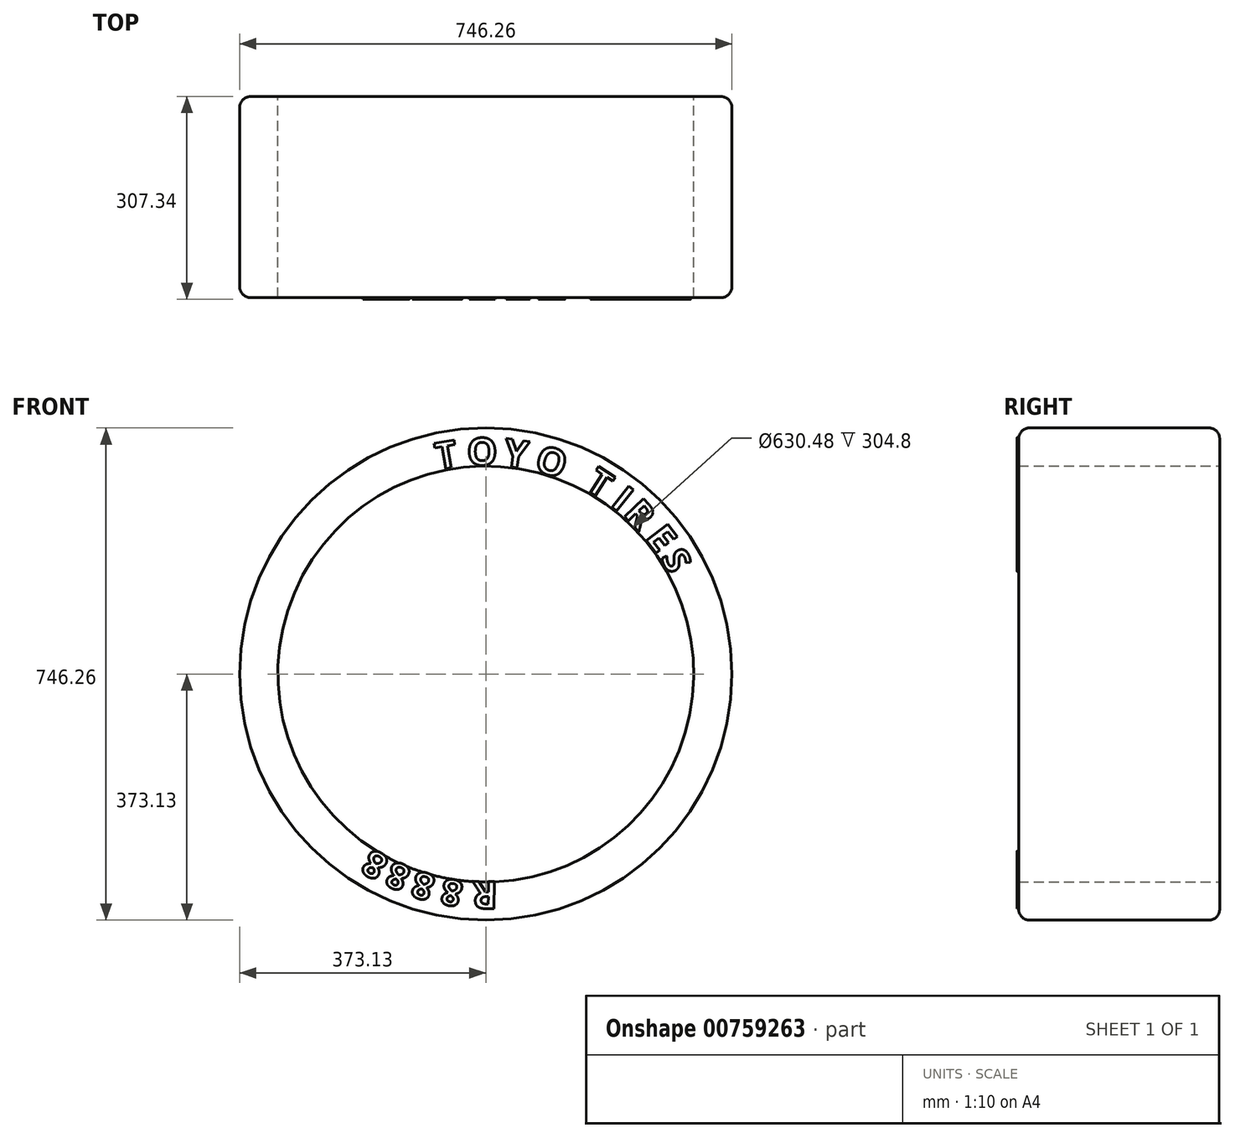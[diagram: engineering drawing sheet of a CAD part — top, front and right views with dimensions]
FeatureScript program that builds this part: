
annotation { "Feature Type Name" : "Feature", "Feature Type Description" : "" }
export const myFeature = defineFeature(function(context is Context, id is Id, definition is map)
    precondition{}
    {
        {
            var Q0;
            Q0=qCreatedBy(makeId("Front.planeOp"),FACE);
            var sketch = newSketch(context, id + "F0", { "sketchPlane" : qUnion([Q0])});
            skCircle(sketch, "E0", {"center": v(0, 0) * mm, "radius": 373.13 * mm});
            skCircle(sketch, "E1", {"center": v(0, 0) * mm, "radius": 315.24 * mm});
            skSolve(sketch);
        }
        {
            var Q0;
            Q0=makeQuery(id+"F0.imprint","IMPRINT",FACE,{"disambiguationData":[TD([[makeQuery(id+"F0.imprint","IMPRINT",EDGE,{"derivedFrom":sQuery(id+"F0.wireOp",EDGE,"E0")}),1.0]])]});
            extrude(context, id + "F1", {"entities" : qUnion([Q0]), "depth" : 304.8 * mm, "offsetDistance" : 25.4 * mm});
        }
        {
            var Q0;
            Q0=makeQuery(id+"F1.opExtrude","CAP_EDGE",EDGE,{"disambiguationData":[OSD([sQuery(id+"F0.wireOp",EDGE,"E0")])],"isStart":false});
            var Q1;
            Q1=makeQuery(id+"F1.opExtrude","CAP_EDGE",EDGE,{"disambiguationData":[OSD([sQuery(id+"F0.wireOp",EDGE,"E0")])],"isStart":true});
            fillet(context, id + "F2", {"entities" : qUnion([Q0, Q1]), "radius" : 16.5 * mm, "tangentPropagation" : true, "allowEdgeOverflow" : false});
        }
        {
            var Q0;
            Q0=makeQuery(id+"F1.opExtrude","CAP_FACE",FACE,{"disambiguationData":[OSD([sQuery(id+"F0.wireOp",EDGE,"E0"),sQuery(id+"F0.wireOp",EDGE,"E1")])],"isStart":false});
            var sketch = newSketch(context, id + "F3", { "sketchPlane" : qUnion([Q0])});
            skText(sketch, "E2", { "text": "T", "fontName": "OpenSans-Bold.ttf"});
            skText(sketch, "E3", { "text": "O", "fontName": "OpenSans-Bold.ttf"});
            skText(sketch, "E4", { "text": "Y", "fontName": "OpenSans-Bold.ttf"});
            skText(sketch, "E5", { "text": "O", "fontName": "OpenSans-Bold.ttf"});
            skText(sketch, "E6", { "text": "T", "fontName": "OpenSans-Bold.ttf"});
            skText(sketch, "E7", { "text": "I", "fontName": "OpenSans-Bold.ttf"});
            skText(sketch, "E8", { "text": "R", "fontName": "OpenSans-Bold.ttf"});
            skText(sketch, "E9", { "text": "E", "fontName": "OpenSans-Bold.ttf"});
            skText(sketch, "E10", { "text": "S", "fontName": "OpenSans-Bold.ttf"});
            const initialGuessF3  = {"E2": [-0.0729, 0.30943, 0.98615, 0.16583, 0.0411], "E3": [-0.02809, 0.31635, 0.99988, 0.01557, 0.04148], "E4": [0.02539, 0.31632, 0.99047, -0.13775, 0.04168], "E5": [0.07182, 0.30945, 0.95338, -0.30178, 0.04132], "E6": [0.14827, 0.28111, 0.8471, -0.53142, 0.04094], "E7": [0.1873, 0.25596, 0.78474, -0.61982, 0.04132], "E8": [0.207, 0.2421, 0.68615, -0.72746, 0.04001], "E9": [0.24018, 0.20625, 0.6097, -0.79263, 0.04154], "E10": [0.26457, 0.17709, 0.45643, -0.88976, 0.0397]};
            skSetInitialGuess(sketch, initialGuessF3);
            skSolve(sketch);
        }
        {
            var Q0;
            Q0 = qSketchRegion(id + "F3", true);
            extrude(context, id + "F4", {"entities" : qUnion([Q0]), "depth" : 2.54 * mm, "offsetDistance" : 25.4 * mm});
        }
        {
            var Q0;
            Q0=makeQuery(id+"F1.opExtrude","CAP_FACE",FACE,{"disambiguationData":[OSD([sQuery(id+"F0.wireOp",EDGE,"E0"),sQuery(id+"F0.wireOp",EDGE,"E1")])],"isStart":false});
            var sketch = newSketch(context, id + "F5", { "sketchPlane" : qUnion([Q0])});
            skText(sketch, "E11", { "text": "R", "fontName": "OpenSans-Bold.ttf"});
            skText(sketch, "E12", { "text": "8", "fontName": "OpenSans-Bold.ttf"});
            skText(sketch, "E13", { "text": "8", "fontName": "OpenSans-Bold.ttf"});
            skText(sketch, "E14", { "text": "8", "fontName": "OpenSans-Bold.ttf"});
            skText(sketch, "E15", { "text": "8", "fontName": "OpenSans-Bold.ttf"});
            const initialGuessF5  = {"E11": [0.0183, -0.3147, -0.99985, 0.01726, 0.0418], "E12": [-0.0324, -0.3155, -0.97743, 0.21124, 0.03966], "E13": [-0.07413, -0.30663, -0.95604, 0.29323, 0.04063], "E14": [-0.11128, -0.29462, -0.91905, 0.39415, 0.03997], "E15": [-0.1446, -0.27985, -0.86574, 0.5005, 0.04078]};
            skSetInitialGuess(sketch, initialGuessF5);
            skSolve(sketch);
        }
        {
            var Q0;
            Q0 = qSketchRegion(id + "F5", true);
            extrude(context, id + "F6", {"entities" : qUnion([Q0]), "depth" : 2.54 * mm, "offsetDistance" : 25.4 * mm});
        }
    });
